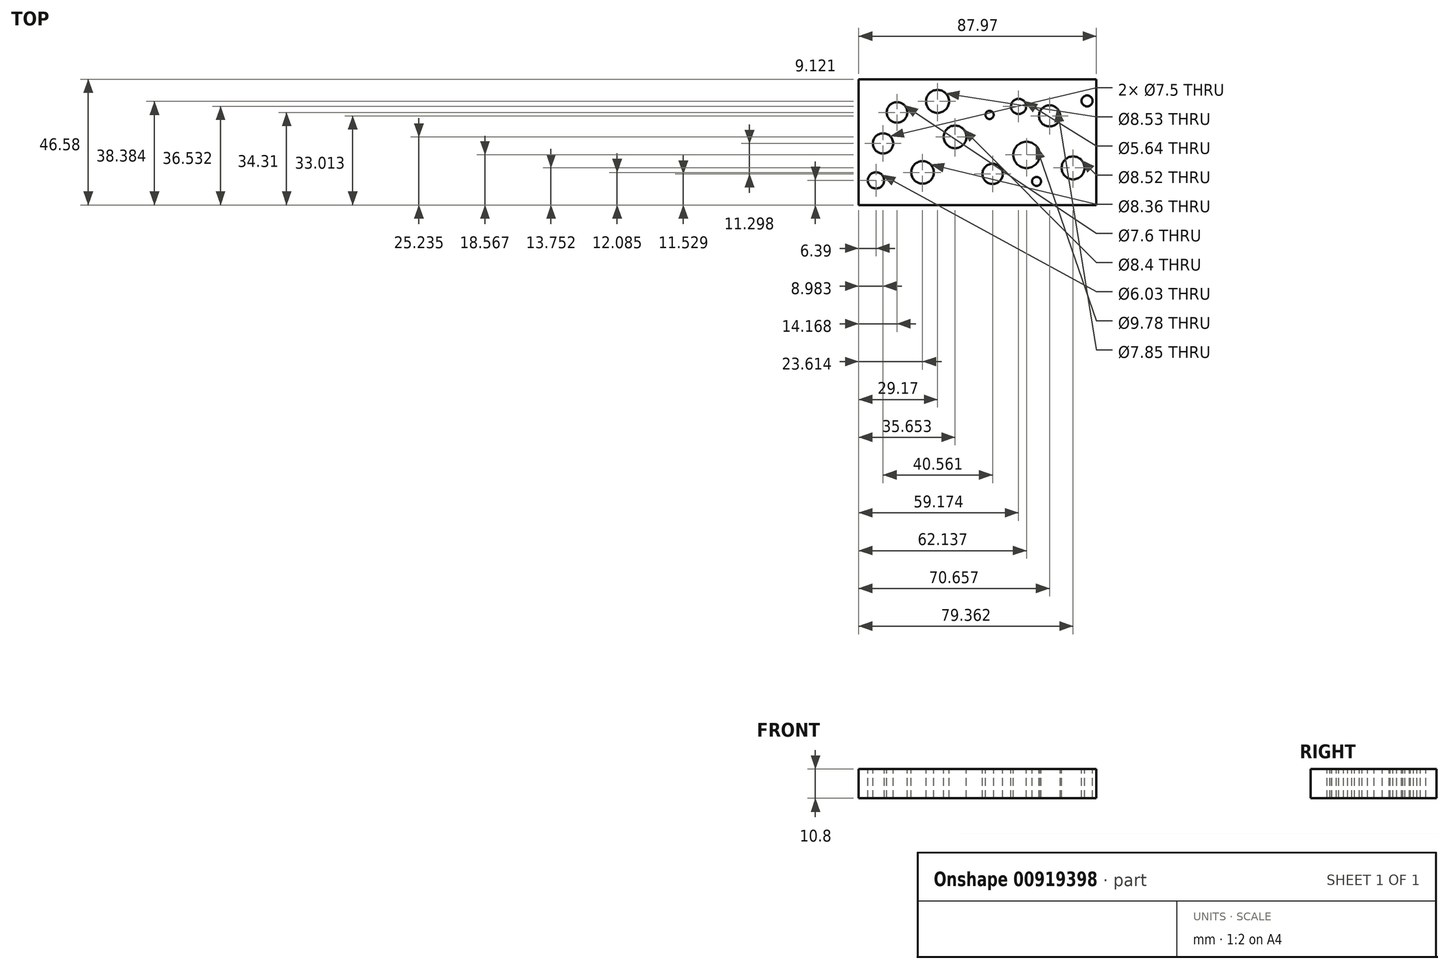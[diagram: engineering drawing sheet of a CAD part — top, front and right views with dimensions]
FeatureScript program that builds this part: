
annotation { "Feature Type Name" : "Feature", "Feature Type Description" : "" }
export const myFeature = defineFeature(function(context is Context, id is Id, definition is map)
    precondition{}
    {
        {
            var Q0;
            Q0=qCreatedBy(makeId("Top.planeOp"),FACE);
            var sketch = newSketch(context, id + "F0", { "sketchPlane" : qUnion([Q0])});
            skLineSegment(sketch, "E0.bottom", {"start": v(0, 0) * mm, "end": v(87.97, 0) * mm});
            skLineSegment(sketch, "E0.top", {"start": v(0, 46.58) * mm, "end": v(87.97, 46.58) * mm});
            skLineSegment(sketch, "E0.left", {"start": v(0, 0) * mm, "end": v(0, 46.58) * mm});
            skLineSegment(sketch, "E0.right", {"start": v(87.97, 0) * mm, "end": v(87.97, 46.58) * mm});
            skSolve(sketch);
        }
        {
            var Q0;
            Q0=makeQuery(id+"F0.imprint","IMPRINT",FACE,{"disambiguationData":[TD([[makeQuery(id+"F0.imprint","IMPRINT",EDGE,{"derivedFrom":sQuery(id+"F0.wireOp",EDGE,"E0.bottom")}),1.0]])]});
            extrude(context, id + "F1", {"entities" : qUnion([Q0]), "oppositeDirection" : true, "depth" : 10.8 * mm, "offsetDistance" : 25 * mm});
        }
        {
            var Q0;
            Q0=makeQuery(id+"F1.opExtrude","CAP_FACE",FACE,{"disambiguationData":[OSD([sQuery(id+"F0.wireOp",EDGE,"E0.bottom"),sQuery(id+"F0.wireOp",EDGE,"E0.top"),sQuery(id+"F0.wireOp",EDGE,"E0.left"),sQuery(id+"F0.wireOp",EDGE,"E0.right")])],"isStart":true});
            var sketch = newSketch(context, id + "F2", { "sketchPlane" : qUnion([Q0])});
            skCircle(sketch, "E1", {"center": v(14.17, 34.3) * mm, "radius": 3.8 * mm});
            skCircle(sketch, "E2", {"center": v(48.43, 33.38) * mm, "radius": 1.53 * mm});
            skCircle(sketch, "E3", {"center": v(35.65, 25.23) * mm, "radius": 4.2 * mm});
            skCircle(sketch, "E4", {"center": v(70.66, 33.01) * mm, "radius": 3.92 * mm});
            skCircle(sketch, "E5", {"center": v(62.14, 18.57) * mm, "radius": 4.89 * mm});
            skCircle(sketch, "E6", {"center": v(23.61, 12.08) * mm, "radius": 4.18 * mm});
            skCircle(sketch, "E7", {"center": v(8.98, 22.83) * mm, "radius": 3.75 * mm});
            skCircle(sketch, "E8", {"center": v(29.17, 38.38) * mm, "radius": 4.26 * mm});
            skCircle(sketch, "E9", {"center": v(49.54, 11.53) * mm, "radius": 3.75 * mm});
            skCircle(sketch, "E10", {"center": v(59.17, 36.53) * mm, "radius": 2.82 * mm});
            skCircle(sketch, "E11", {"center": v(84.55, 38.57) * mm, "radius": 2.04 * mm});
            skCircle(sketch, "E12", {"center": v(79.36, 13.75) * mm, "radius": 4.26 * mm});
            skCircle(sketch, "E13", {"center": v(65.84, 8.75) * mm, "radius": 1.66 * mm});
            skCircle(sketch, "E14", {"center": v(6.39, 9.12) * mm, "radius": 3.01 * mm});
            skSolve(sketch);
        }
        {
            var Q0;
            Q0=makeQuery(id+"F2.imprint","IMPRINT",FACE,{"disambiguationData":[TD([[makeQuery(id+"F2.imprint","IMPRINT",EDGE,{"derivedFrom":sQuery(id+"F2.wireOp",EDGE,"E8")}),1.0]])]});
            var Q1;
            Q1=makeQuery(id+"F2.imprint","IMPRINT",FACE,{"disambiguationData":[TD([[makeQuery(id+"F2.imprint","IMPRINT",EDGE,{"derivedFrom":sQuery(id+"F2.wireOp",EDGE,"E3")}),1.0]])]});
            var Q2;
            Q2=makeQuery(id+"F2.imprint","IMPRINT",FACE,{"disambiguationData":[TD([[makeQuery(id+"F2.imprint","IMPRINT",EDGE,{"derivedFrom":sQuery(id+"F2.wireOp",EDGE,"E7")}),1.0]])]});
            var Q3;
            Q3=makeQuery(id+"F2.imprint","IMPRINT",FACE,{"disambiguationData":[TD([[makeQuery(id+"F2.imprint","IMPRINT",EDGE,{"derivedFrom":sQuery(id+"F2.wireOp",EDGE,"E1")}),1.0]])]});
            var Q4;
            Q4=makeQuery(id+"F2.imprint","IMPRINT",FACE,{"disambiguationData":[TD([[makeQuery(id+"F2.imprint","IMPRINT",EDGE,{"derivedFrom":sQuery(id+"F2.wireOp",EDGE,"E6")}),1.0]])]});
            var Q5;
            Q5=makeQuery(id+"F2.imprint","IMPRINT",FACE,{"disambiguationData":[TD([[makeQuery(id+"F2.imprint","IMPRINT",EDGE,{"derivedFrom":sQuery(id+"F2.wireOp",EDGE,"E14")}),1.0]])]});
            var Q6;
            Q6=makeQuery(id+"F2.imprint","IMPRINT",FACE,{"disambiguationData":[TD([[makeQuery(id+"F2.imprint","IMPRINT",EDGE,{"derivedFrom":sQuery(id+"F2.wireOp",EDGE,"E9")}),1.0]])]});
            var Q7;
            Q7=makeQuery(id+"F2.imprint","IMPRINT",FACE,{"disambiguationData":[TD([[makeQuery(id+"F2.imprint","IMPRINT",EDGE,{"derivedFrom":sQuery(id+"F2.wireOp",EDGE,"E5")}),1.0]])]});
            var Q8;
            Q8=makeQuery(id+"F2.imprint","IMPRINT",FACE,{"disambiguationData":[TD([[makeQuery(id+"F2.imprint","IMPRINT",EDGE,{"derivedFrom":sQuery(id+"F2.wireOp",EDGE,"E4")}),1.0]])]});
            var Q9;
            Q9=makeQuery(id+"F2.imprint","IMPRINT",FACE,{"disambiguationData":[TD([[makeQuery(id+"F2.imprint","IMPRINT",EDGE,{"derivedFrom":sQuery(id+"F2.wireOp",EDGE,"E11")}),1.0]])]});
            var Q10;
            Q10=makeQuery(id+"F2.imprint","IMPRINT",FACE,{"disambiguationData":[TD([[makeQuery(id+"F2.imprint","IMPRINT",EDGE,{"derivedFrom":sQuery(id+"F2.wireOp",EDGE,"E10")}),1.0]])]});
            var Q11;
            Q11=makeQuery(id+"F2.imprint","IMPRINT",FACE,{"disambiguationData":[TD([[makeQuery(id+"F2.imprint","IMPRINT",EDGE,{"derivedFrom":sQuery(id+"F2.wireOp",EDGE,"E2")}),1.0]])]});
            var Q12;
            Q12=makeQuery(id+"F2.imprint","IMPRINT",FACE,{"disambiguationData":[TD([[makeQuery(id+"F2.imprint","IMPRINT",EDGE,{"derivedFrom":sQuery(id+"F2.wireOp",EDGE,"E13")}),1.0]])]});
            var Q13;
            Q13=makeQuery(id+"F2.imprint","IMPRINT",FACE,{"disambiguationData":[TD([[makeQuery(id+"F2.imprint","IMPRINT",EDGE,{"derivedFrom":sQuery(id+"F2.wireOp",EDGE,"E12")}),1.0]])]});
            extrude(context, id + "F3", {"entities" : qUnion([Q0, Q1, Q2, Q3, Q4, Q5, Q6, Q7, Q8, Q9, Q10, Q11, Q12, Q13]), "operationType" : NewBodyOperationType.REMOVE, "oppositeDirection" : true, "depth" : 25 * mm, "offsetDistance" : 25 * mm});
        }
    });
